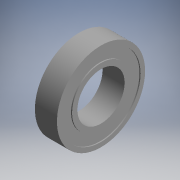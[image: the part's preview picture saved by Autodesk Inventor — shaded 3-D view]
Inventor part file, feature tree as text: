
AUTODESK INVENTOR PART (.ipt)
format: ipt  version: 2017.3 (Build 213256000, 256)  size: 115,712 bytes
history: native  units: mm (DEFAULTED — no unit token found)
features: other x7, revolve x1, sketch x1
ambient origin geometry x8: Origin, YZ Plane, XZ Plane, XY Plane, X Axis, Y Axis, Z Axis, Center Point
bodies: Solid1 (feature_tree)
feature tree (9):
  revolve  "Revolution1"  [1 undecoded]
  other  "to_cp1_XY"
  other  "to_cp1_YZ"
  other  "to_cp1_ZX"
  other  "to_cp1_X"
  other  "to_cp1_Y"
  other  "to_cp1_Z"
  other  "to_cp1_Center"
  sketch  "Sketch_1"  dims[d0=360.0deg d1=0.0mm]
note: 1 required parameter value undecoded (feature->parameter linkage not recoverable at this tier; creation-order binding heuristic only, values carry confidence <= 0.55)
